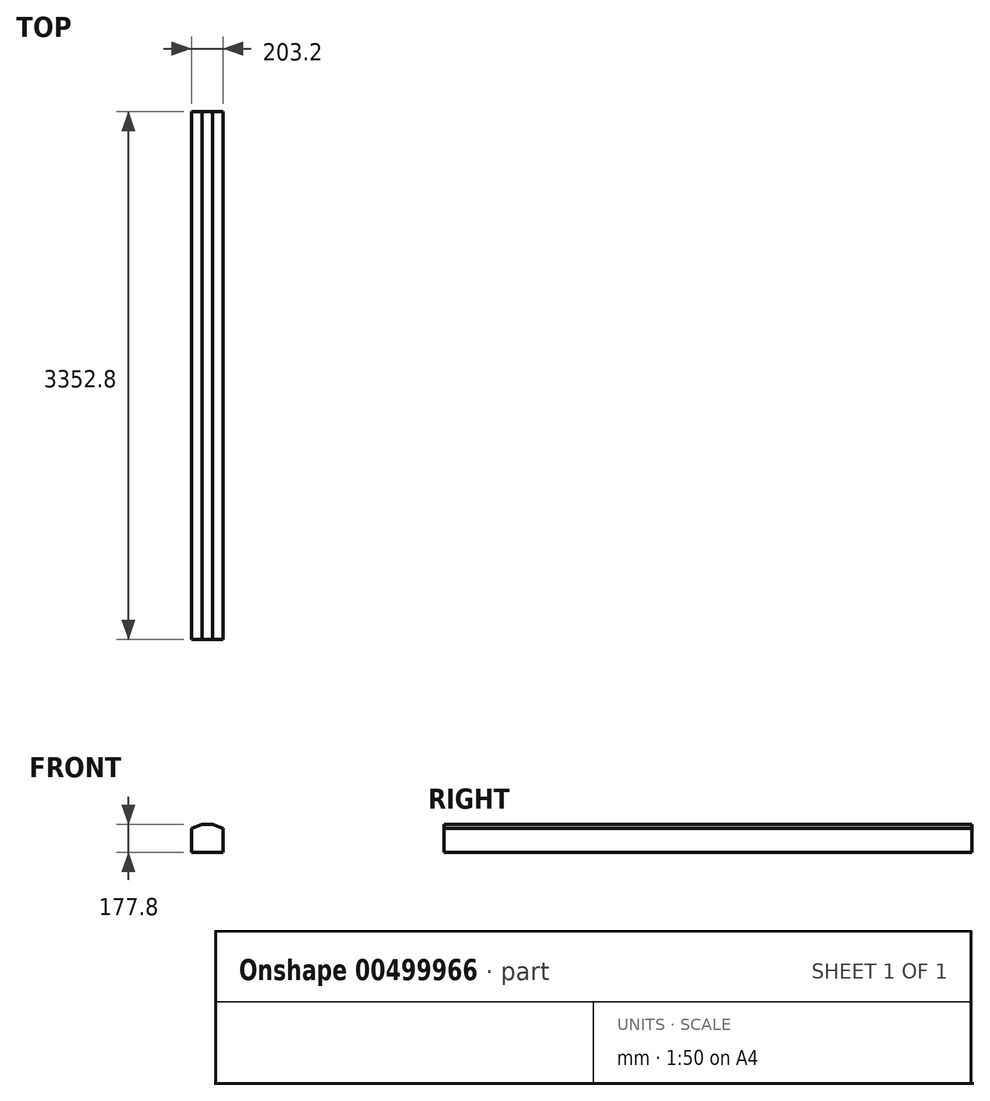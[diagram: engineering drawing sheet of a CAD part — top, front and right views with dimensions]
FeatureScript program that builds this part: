
annotation { "Feature Type Name" : "Feature", "Feature Type Description" : "" }
export const myFeature = defineFeature(function(context is Context, id is Id, definition is map)
    precondition{}
    {
        {
            var Q0;
            Q0=qCreatedBy(makeId("Right.planeOp"),FACE);
            var sketch = newSketch(context, id + "F0", { "sketchPlane" : qUnion([Q0])});
            skLineSegment(sketch, "E0.bottom", {"start": v(1676.4, 88.9) * mm, "end": v(-1676.4, 88.9) * mm});
            skLineSegment(sketch, "E0.top", {"start": v(1676.4, -88.9) * mm, "end": v(-1676.4, -88.9) * mm});
            skLineSegment(sketch, "E0.left", {"start": v(1676.4, 88.9) * mm, "end": v(1676.4, -88.9) * mm});
            skLineSegment(sketch, "E0.right", {"start": v(-1676.4, 88.9) * mm, "end": v(-1676.4, -88.9) * mm});
            skPoint(sketch, "E0.middle", {"position": v(0, 0) * mm});
            skSolve(sketch);
        }
        {
            var Q0;
            Q0 = qSketchRegion(id + "F0", true);
            extrude(context, id + "F1", {"entities" : qUnion([Q0]), "endBound" : BoundingType.SYMMETRIC, "depth" : 203.2 * mm, "offsetDistance" : 25.4 * mm});
        }
        {
            var Q0;
            Q0=makeQuery(id+"F1.opExtrude","SWEPT_FACE",FACE,{"disambiguationData":[OSD([sQuery(id+"F0.wireOp",EDGE,"E0.right")])]});
            var sketch = newSketch(context, id + "F2", { "sketchPlane" : qUnion([Q0])});
            skLineSegment(sketch, "E1", {"start": v(-101.6, 63.5) * mm, "end": v(-31.75, 88.9) * mm});
            skLineSegment(sketch, "E2", {"start": v(101.6, 63.5) * mm, "end": v(31.75, 88.9) * mm});
            skSolve(sketch);
        }
        {
            var Q0;
            Q0 = qSketchRegion(id + "F2", true);
            var Q1;
            {var subQ0=sQuery(id+"F2.wireOp",EDGE,"E1");Q1=makeQuery(id+"F2.imprint","IMPRINT",FACE,{"disambiguationData":[TD([[makeQuery(id+"F2.imprint","IMPRINT",EDGE,{"derivedFrom":subQ0}),1.0]])]});}
            var Q2;
            {var subQ0=sQuery(id+"F2.wireOp",EDGE,"E2");Q2=makeQuery(id+"F2.imprint","IMPRINT",FACE,{"disambiguationData":[TD([[makeQuery(id+"F2.imprint","IMPRINT",EDGE,{"derivedFrom":subQ0}),-1.0]])]});}
            extrude(context, id + "F3", {"entities" : qUnion([Q0, Q1, Q2]), "operationType" : NewBodyOperationType.REMOVE, "oppositeDirection" : true, "depth" : 3352.8 * mm, "offsetDistance" : 25.4 * mm});
        }
    });
